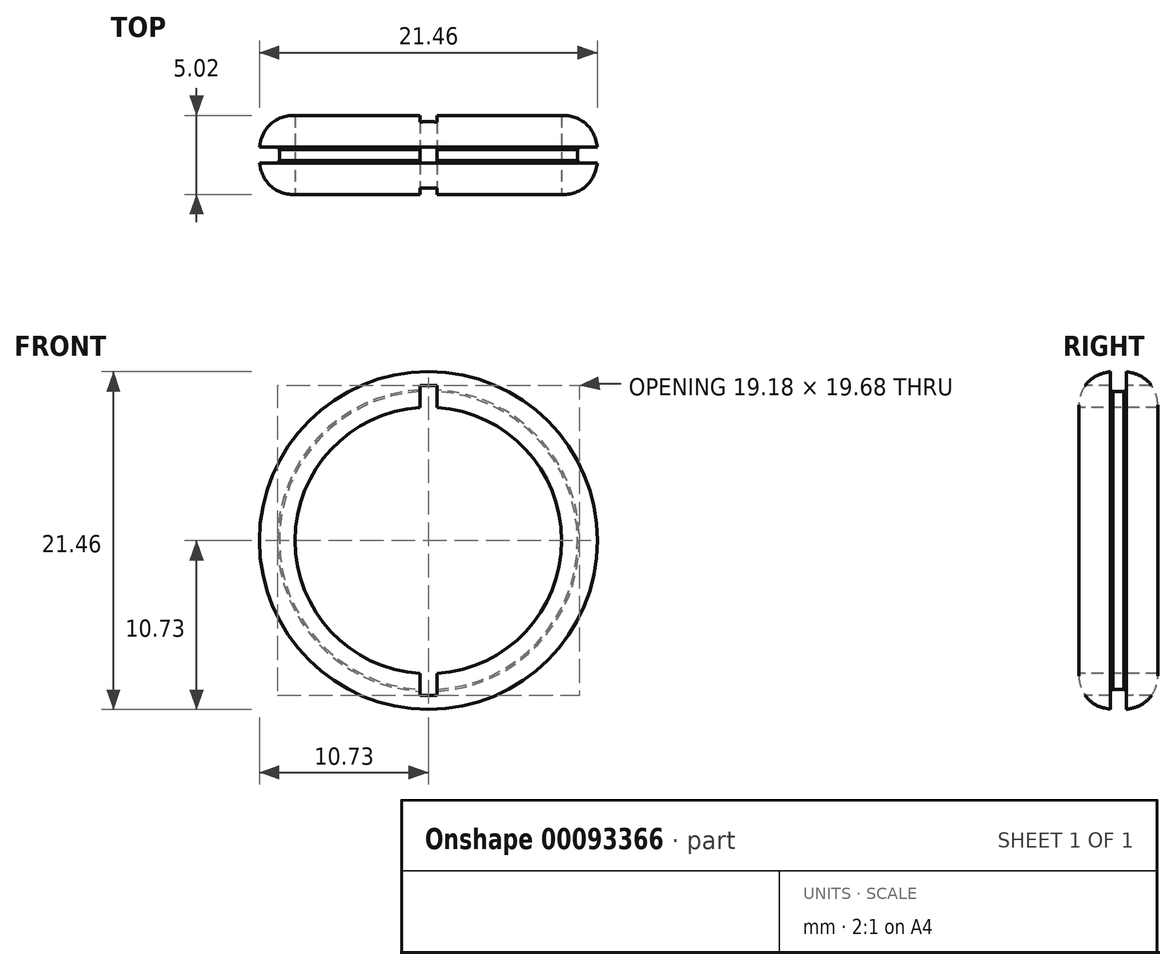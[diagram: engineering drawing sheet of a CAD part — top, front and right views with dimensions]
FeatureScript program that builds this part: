
annotation { "Feature Type Name" : "Feature", "Feature Type Description" : "" }
export const myFeature = defineFeature(function(context is Context, id is Id, definition is map)
    precondition{}
    {
        {
            var Q0;
            Q0=qCreatedBy(makeId("Front.planeOp"),FACE);
            var sketch = newSketch(context, id + "F0", { "sketchPlane" : qUnion([Q0])});
            skCircle(sketch, "E0", {"center": v(0, 0) * mm, "radius": 8.65 * mm});
            skPoint(sketch, "E1", {"position": v(0, 8.65) * mm});
            skSolve(sketch);
        }
        {
            var Q0;
            Q0=qCreatedBy(makeId("Right.planeOp"),FACE);
            var sketch = newSketch(context, id + "F1", { "sketchPlane" : qUnion([Q0])});
            skLineSegment(sketch, "E2", {"start": v(0, 8.47) * mm, "end": v(-2.5, 8.47) * mm});
            skLineSegment(sketch, "E3", {"start": v(-2.5, 8.47) * mm, "end": v(-2.64, 10.25) * mm});
            skLineSegment(sketch, "E4", {"start": v(-2.64, 10.25) * mm, "end": v(-0.5, 10.73) * mm});
            skLineSegment(sketch, "E5", {"start": v(-0.5, 10.73) * mm, "end": v(-0.5, 9.59) * mm});
            skLineSegment(sketch, "E6", {"start": v(-0.5, 9.59) * mm, "end": v(-0.34, 9.47) * mm});
            skLineSegment(sketch, "E7", {"start": v(-0.34, 9.47) * mm, "end": v(0, 9.47) * mm});
            skLineSegment(sketch, "E8.MirrorCS", {"start": v(0.5, 9.59) * mm, "end": v(0.34, 9.47) * mm});
            skLineSegment(sketch, "E9.MirrorCS", {"start": v(2.64, 10.25) * mm, "end": v(0.5, 10.73) * mm});
            skLineSegment(sketch, "E10.MirrorCS", {"start": v(0.5, 10.73) * mm, "end": v(0.5, 9.59) * mm});
            skLineSegment(sketch, "E11.MirrorCS", {"start": v(2.5, 8.47) * mm, "end": v(2.64, 10.25) * mm});
            skLineSegment(sketch, "E12.MirrorCS", {"start": v(0, 8.47) * mm, "end": v(2.5, 8.47) * mm});
            skLineSegment(sketch, "E13.MirrorCS", {"start": v(0.34, 9.47) * mm, "end": v(0, 9.47) * mm});
            skSolve(sketch);
        }
        {
            var Q0;
            Q0=makeQuery(id+"F1.imprint","IMPRINT",FACE,{"disambiguationData":[TD([[makeQuery(id+"F1.imprint","IMPRINT",EDGE,{"derivedFrom":sQuery(id+"F1.wireOp",EDGE,"E2")}),-1.0]])]});
            var Q1;
            Q1=sQuery(id+"F0.wireOp",EDGE,"E0");
            sweep(context, id + "F2", {"profiles" : qUnion([Q0]), "path" : qUnion([Q1])});
        }
        {
            var Q0;
            Q0=makeQuery(id+"F2.opSweep","SWEPT_EDGE",EDGE,{"disambiguationData":[OSD([sQuery(id+"F0.wireOp",EDGE,"E0"),sQuery(id+"F1.wireOp",EDGE,"E3"),sQuery(id+"F1.wireOp",EDGE,"E4")])]});
            var Q1;
            Q1=makeQuery(id+"F2.opSweep","SWEPT_EDGE",EDGE,{"disambiguationData":[OSD([sQuery(id+"F0.wireOp",EDGE,"E0"),sQuery(id+"F1.wireOp",EDGE,"E9.MirrorCS"),sQuery(id+"F1.wireOp",EDGE,"E11.MirrorCS")])]});
            fillet(context, id + "F3", {"entities" : qUnion([Q0, Q1]), "radius" : 2.07 * mm, "tangentPropagation" : true, "allowEdgeOverflow" : false});
        }
        {
            var Q0;
            Q0=qCreatedBy(makeId("Front.planeOp"),FACE);
            var sketch = newSketch(context, id + "F4", { "sketchPlane" : qUnion([Q0])});
            skLineSegment(sketch, "E14.bottom", {"start": v(-0.54, 9.84) * mm, "end": v(0.54, 9.84) * mm});
            skLineSegment(sketch, "E14.top", {"start": v(-0.54, -9.84) * mm, "end": v(0.54, -9.84) * mm});
            skLineSegment(sketch, "E14.left", {"start": v(-0.54, 9.84) * mm, "end": v(-0.54, -9.84) * mm});
            skLineSegment(sketch, "E14.right", {"start": v(0.54, 9.84) * mm, "end": v(0.54, -9.84) * mm});
            skPoint(sketch, "E14.middle", {"position": v(0, 0) * mm});
            skSolve(sketch);
        }
        {
            var Q0;
            Q0 = qSketchRegion(id + "F4", true);
            extrude(context, id + "F5", {"entities" : qUnion([Q0]), "operationType" : NewBodyOperationType.REMOVE, "oppositeDirection" : true, "depth" : 25 * mm, "hasSecondDirection" : true, "secondDirectionOppositeDirection" : false, "secondDirectionDepth" : 25 * mm});
        }
    });
